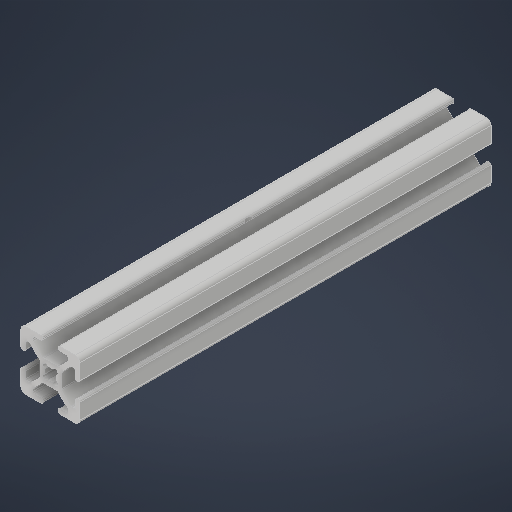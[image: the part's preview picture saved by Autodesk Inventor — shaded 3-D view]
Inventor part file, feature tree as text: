
AUTODESK INVENTOR PART (.ipt)
format: ipt  version: 2025 (Build 290162000, 162)  size: 428,032 bytes
history: native  units: mm
features: extrude x2, sketch x2
ambient origin geometry x8: Origin, YZ Plane, XZ Plane, XY Plane, X Axis, Y Axis, Z Axis, Center Point
bodies: Solid1 (feature_tree)
feature tree (4):
  extrude  "Extrusion1"  Depth=6.0mm
  extrude  "Extrusion2"  [1 undecoded]
  sketch  "Sketch_1"  dims[d0=140.25mm d1=0.0mm d2=6.0mm]
  sketch  "Sketch2"  dims[d3=0.0mm d4=0.0mm]
note: 1 required parameter value undecoded (feature->parameter linkage not recoverable at this tier; creation-order binding heuristic only, values carry confidence <= 0.55)
